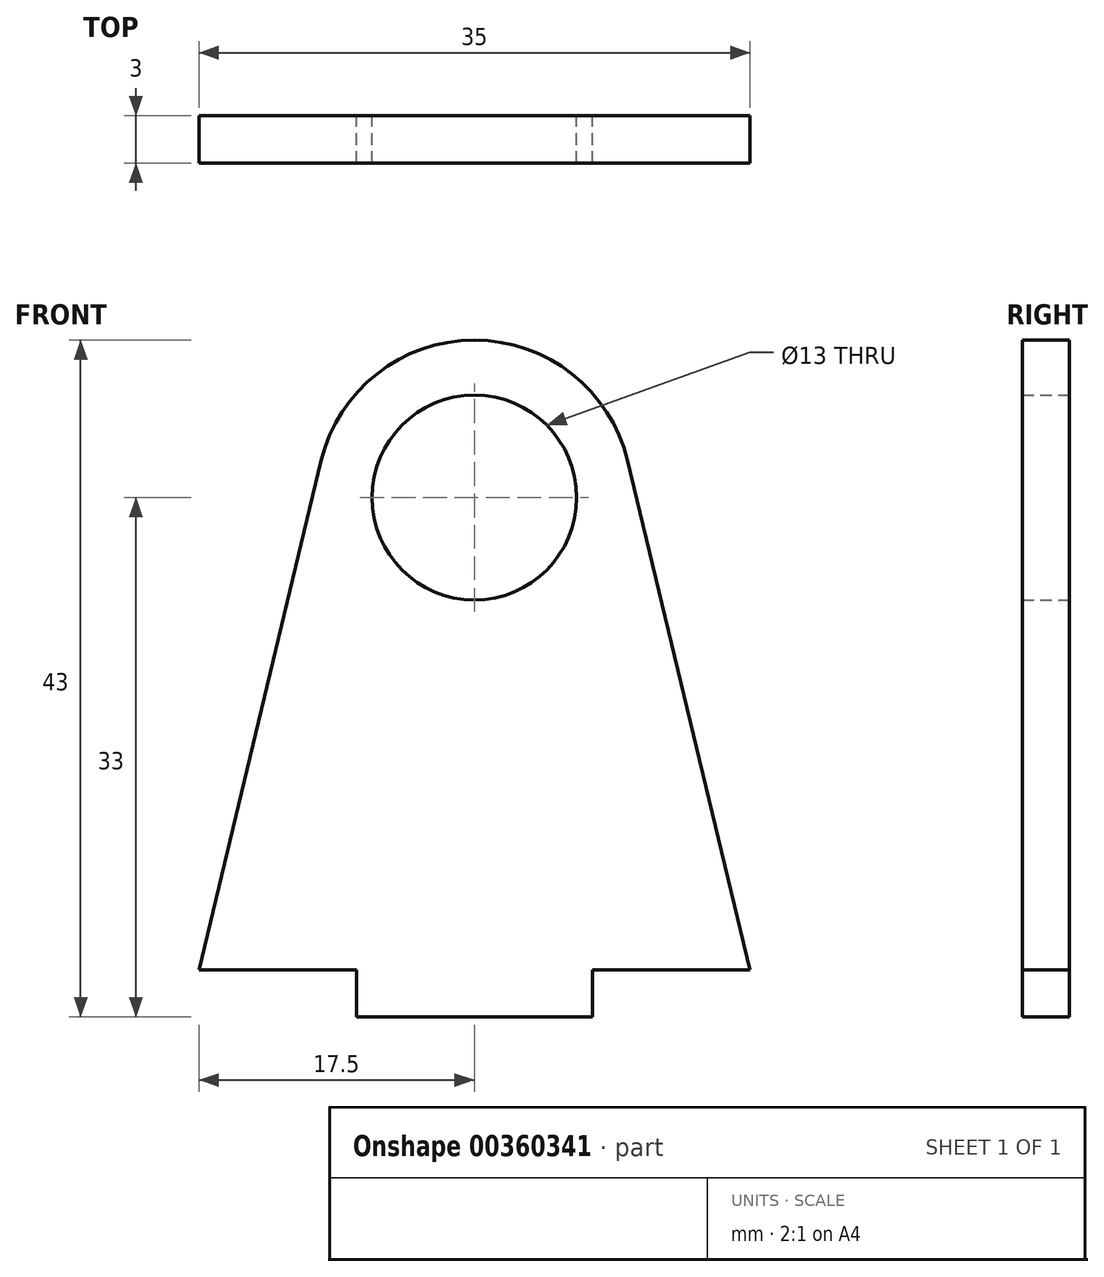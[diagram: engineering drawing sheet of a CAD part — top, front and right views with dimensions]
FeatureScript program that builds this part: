
annotation { "Feature Type Name" : "Feature", "Feature Type Description" : "" }
export const myFeature = defineFeature(function(context is Context, id is Id, definition is map)
    precondition{}
    {
        {
            var Q0;
            Q0=qCreatedBy(makeId("Front.planeOp"),FACE);
            var sketch = newSketch(context, id + "F0", { "sketchPlane" : qUnion([Q0])});
            skLineSegment(sketch, "E0", {"start": v(-9.72, 32.34) * mm, "end": v(-17.5, 0) * mm});
            skLineSegment(sketch, "E1", {"start": v(-17.5, 0) * mm, "end": v(-7.5, 0) * mm});
            skLineSegment(sketch, "E2", {"start": v(-7.5, 0) * mm, "end": v(-7.5, -3) * mm});
            skArc(sketch, "E3", {"start": v(-9.72, 32.34) * mm, "mid": v(-6.19, 37.85) * mm, "end": v(0, 40) * mm});
            skLineSegment(sketch, "E4", {"start": v(-7.5, -3) * mm, "end": v(0, -3) * mm});
            skArc(sketch, "E5", {"start": v(0, 36.5) * mm, "mid": v(-6.5, 30) * mm, "end": v(0, 23.5) * mm});
            skLineSegment(sketch, "E6.MirrorCS", {"start": v(7.5, -3) * mm, "end": v(0, -3) * mm});
            skLineSegment(sketch, "E7.MirrorCS", {"start": v(7.5, 0) * mm, "end": v(7.5, -3) * mm});
            skLineSegment(sketch, "E8.MirrorCS", {"start": v(9.72, 32.34) * mm, "end": v(17.5, 0) * mm});
            skLineSegment(sketch, "E9.MirrorCS", {"start": v(17.5, 0) * mm, "end": v(7.5, 0) * mm});
            skArc(sketch, "E10.MirrorCS", {"start": v(9.72, 32.34) * mm, "mid": v(6.19, 37.85) * mm, "end": v(0, 40) * mm});
            skArc(sketch, "E11.MirrorCS", {"start": v(0, 36.5) * mm, "mid": v(6.5, 30) * mm, "end": v(0, 23.5) * mm});
            skSolve(sketch);
        }
        {
            var Q0;
            Q0=qSketchRegion(id+"F0",true);
            extrude(context, id + "F1", {"entities" : qUnion([Q0]), "depth" : 3 * mm});
        }
    });
